# Revit family: AFX-Axel-LED_Vanity
name_source: partatom
category: Lighting Fixtures
units: mm (PartAtom-declared; Revit-internal decimal feet)

## family parameters
Cut with Voids When Loaded = No
Host = Face
Light Source = Yes
Maintain Annotation Orientation = No
Part Type = Normal
Room Calculation Point = No
Round Connector Dimension = Use Diameter
Shared = No

## types (1)
- AXL4804
    Apparent Load = 0 VA
    Assembly Code = D5020200
    Canopy Finish = AFX - Paint Black
    Color Filter = 16777215
    Default Elevation = 48"
    Depth = 4"
    Description = LED Vanity - 48"L x 4"D x 4 1/8"H
    Diffuser Finish = AFX - Diffuser
    Dimming Lamp Color Temperature Shift = <None>
    Emit Shape Visible in Rendering = No
    Emit from Rectangle Length = 2"
    Emit from Rectangle Width = 47"
    Height = 4 1/8"
    Keynote = 12500
    Length = 48"
    Manufacturer = AFX Inc
    Model = AXL4804
    Photometric Web File = AXLV4804LAJUDSN_3000K_IES.IES
    Power Factor = 1
    Product Documentation Link = https://www.afxinc.com
    Revit Model Built By = https://www.servex-us.com
    Support Finish = AFX - Paint Black
    Sustainability = https://lamprecycle.org
    Tilt Angle = 180.00°
    Type Comments = Axel
    URL = https://www.afxinc.com
    Voltage = 120 V
    Wattage Comments = 40W

## geometry (parser evidence)
native form markers: Sweep x2
no freeform markers — native parametric forms only
